# Revit family: LIXIL - 705429WH - VAAL URINAL
name_source: partatom
category: Plumbing Fixtures
units: mm (PartAtom-declared; Revit-internal decimal feet)

## family parameters
Always vertical = Yes
Cut with Voids When Loaded = No
Enable Cutting in Views = No
Maintain Annotation Orientation = No
OmniClass Number = 23.45.00.00
OmniClass Title = Sanitary, Laundry, and Cleaning Equipment
Part Type = Normal
Room Calculation Point = No
Round Connector Dimension = Use Diameter
Shared = Yes
Work Plane-Based = No

## types (1)
- 705429WH
    CW Connection Diameter = 55 mm
    CW Connection Radius = 28 mm
    Default Elevation = 0 mm  [stored 0 ft]
    Description = Vaal Urinal to detail and spec. See sanware schedule. Available from Lixil.
    Hosted on lixil.co.za = https://www.lixil.co.za
    M _ FLUSH UNIT = M _ LIXIL - STAINLESS STEEL 01
    M _ URINAL = M _ LIXIL - VAAL - PORCELAIN - WHITE 01
    Product Specification = Supplier: Lixil.
Product Description: Vaal Flatback top-entry urinal. Spreader & fittings included. Suitable for commercial use. Compatible with the following Cobra exposed urinal flush valves: FJ6-000/N & FJ6-001/N. Dimensions: 300mm long, 315mm wide, 450mm high. 10 Year LIXIL Africa warranty. Access to Cobra TeamAssist technical team.
10 Year Warranty 
Product Code: 1046400200.
SKU Code	: 705429WH.
Barcode: 6005826072914.
Brand: Vaal.
Range: Vaal.
Category: Plumbing Supplies.
Sub-Category: Urinals.
Material: Ceramic.
Colour: White.
Package Height: 450 mm
Package Width: 315 mm
Package Length: 300 mm
Product Height: 450mm
Product Width: 315 mm
Product Length: 300 mm
Package Volume: 42525000 mm³.
Package Weight: 10.94 kg

Notes:
- Refer to manufacturer's and supplier's installation, maintenance and cleaning manual.
- Refer to manufacturer's and supplier's guarantees and warrantees document.
    Waste Connection Diameter = 102 mm
    Waste Connection Radius = 51 mm

note: [stored X ft] marks values corroborated as IEEE doubles in the binary element streams (Revit-internal decimal feet)

## geometry (parser evidence)
native form markers: Sweep x10
no freeform markers — native parametric forms only
